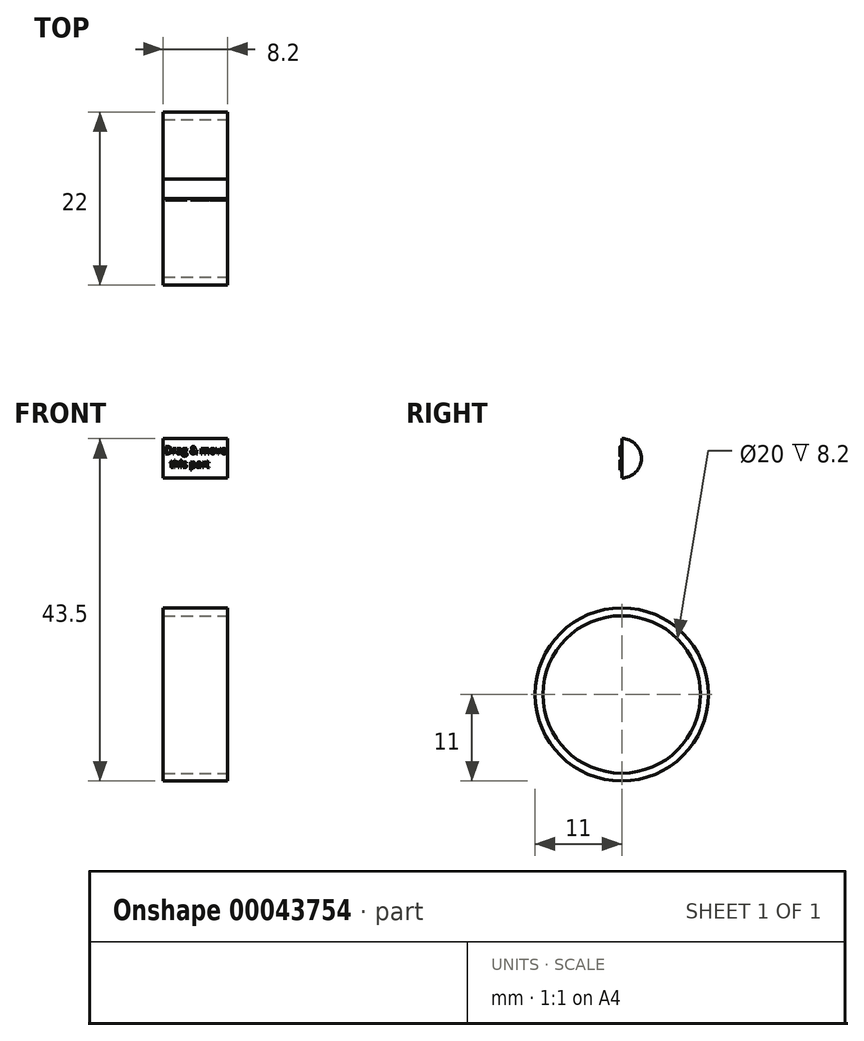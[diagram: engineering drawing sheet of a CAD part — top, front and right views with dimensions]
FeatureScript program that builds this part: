
annotation { "Feature Type Name" : "Feature", "Feature Type Description" : "" }
export const myFeature = defineFeature(function(context is Context, id is Id, definition is map)
    precondition{}
    {
        {
            var Q0;
            Q0=qCreatedBy(makeId("Right.planeOp"),FACE);
            var sketch = newSketch(context, id + "F0", { "sketchPlane" : qUnion([Q0])});
            skCircle(sketch, "E0", {"center": v(0, 0) * mm, "radius": 10 * mm});
            skCircle(sketch, "E1", {"center": v(0, 0) * mm, "radius": 11 * mm});
            skArc(sketch, "E2", {"start": v(0, 27.5) * mm, "mid": v(2.5, 30) * mm, "end": v(0, 32.5) * mm});
            skLineSegment(sketch, "E3", {"start": v(0, 32.5) * mm, "end": v(0, 27.5) * mm});
            skSolve(sketch);
        }
        {
            var Q0;
            Q0 = qSketchRegion(id + "F0", true);
            extrude(context, id + "F1", {"entities" : qUnion([Q0]), "oppositeDirection" : true, "depth" : 8.2 * mm});
        }
        {
            var Q0;
            Q0=makeQuery(id+"F1.opExtrude","SWEPT_FACE",FACE,{"disambiguationData":[OSD([sQuery(id+"F0.wireOp",EDGE,"E3")])]});
            var sketch = newSketch(context, id + "F2", { "sketchPlane" : qUnion([Q0])});
            skText(sketch, "E4", { "text": "Drag & move\n  this part", "fontName": "OpenSans-Regular.ttf"});
            const initialGuessF2  = {"E4": [-0.008, 0.03057, 1, 0, 0.00093]};
            skSetInitialGuess(sketch, initialGuessF2);
            skSolve(sketch);
        }
        {
            var Q0;
            Q0 = qSketchRegion(id + "F2", true);
            extrude(context, id + "F3", {"entities" : qUnion([Q0]), "operationType" : NewBodyOperationType.ADD, "depth" : 0.2 * mm});
        }
    });
